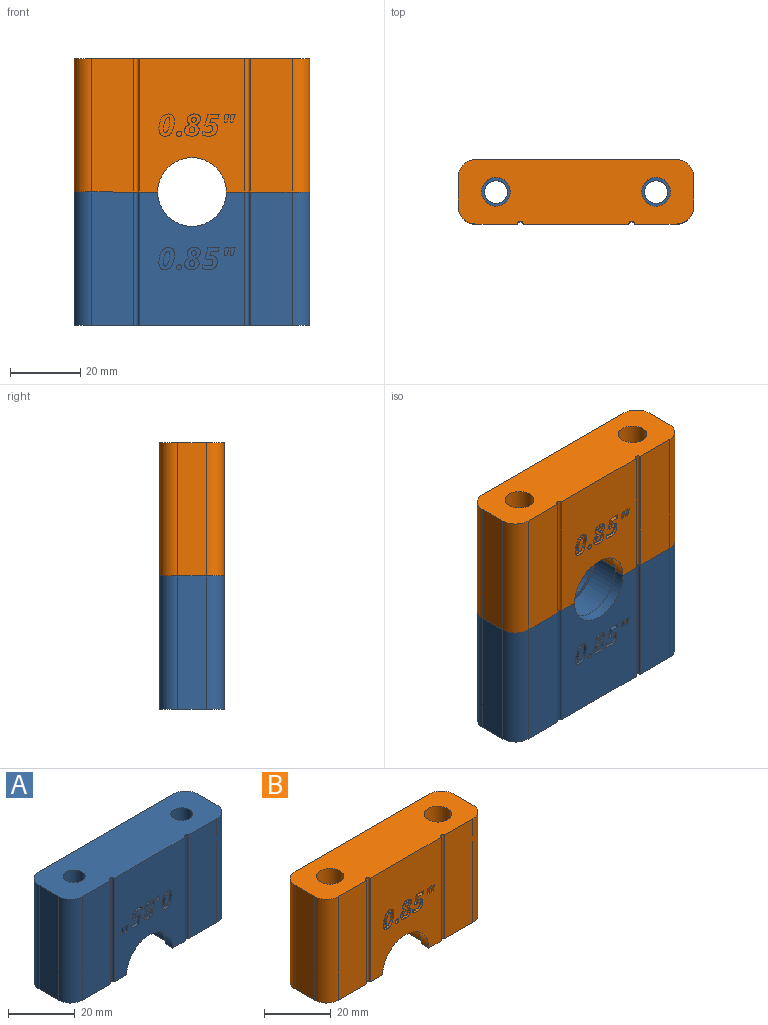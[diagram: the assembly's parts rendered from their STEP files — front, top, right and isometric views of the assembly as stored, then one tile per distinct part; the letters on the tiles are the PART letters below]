
ASSEMBLY  parts=2 mates=1
PART A: 116 faces, bbox 67.3x18.4x38.1 mm
  f0: plane 38.1x30.15mm, normal (0,-1,0), area 935mm2, adj f1,f2,f3,f13,f14,f15,f18,f19
  f1: plane 23.88x18.42mm, normal (0,0,-1), area 385.1mm2, adj f0,f5,f6,f7,f9,f10,f11,f12
  f2: plane 67.31x18.42mm, normal (0,0,1), area 1148.4mm2, adj f0,f4,f5,f7,f8,f10,f14,f15
  f3: plane 23.88x18.42mm, normal (0,0,-1), area 385.1mm2, adj f0,f4,f6,f8,f9,f10,f11,f12
  f4: plane 38.1x11.9mm, normal (0,-1,0), area 453.4mm2, adj f2,f3,f14,f112
  f5: plane 38.1x11.9mm, normal (0,-1,0), area 453.4mm2, adj f1,f2,f15,f113
  f6: plane 21.59x10.8mm, normal (0,-1,0), area 32.8mm2, adj f1,f3,f9,f11
  f7: plane 38.1x8.26mm, normal (1,0,0), area 314.5mm2, adj f1,f2,f113,f115
  f8: plane 38.1x8.26mm, normal (-1,0,0), area 314.5mm2, adj f2,f3,f112,f114
  f9: cylinder r=9.78mm len=19.56mm, axis (0,-1,0), area 195.1mm2, adj f1,f3,f6,f10
  f10: plane 57.15x38.1mm, normal (0,1,0), area 2027.2mm2, adj f1,f2,f3,f9,f114,f115
  f11: cylinder r=10.79mm len=21.59mm, axis (0,-1,0), area 301.5mm2, adj f1,f3,f6,f12
  f12: plane 21.59x10.8mm, normal (0,1,0), area 32.8mm2, adj f1,f3,f11,f13
  f13: cylinder r=9.78mm len=19.56mm, axis (0,-1,0), area 97.5mm2, adj f0,f1,f3,f12
  f14: cylinder r=0.8mm len=38.1mm, axis (0,0,-1), area 95.8mm2, adj f0,f2,f3,f4
  f15: cylinder r=0.8mm len=38.1mm, axis (0,0,-1), area 95.8mm2, adj f0,f1,f2,f5
  f16: cylinder r=3.26mm len=38.1mm, axis (0,0,-1), area 781.3mm2, adj f2,f3
  f17: cylinder r=3.26mm len=38.1mm, axis (0,0,-1), area 781.3mm2, adj f1,f2
  f18: plane 1.02x0.84mm, normal (0,0,-1), area 0.9mm2, adj f0,f19,f21,f22
  f19: plane 2.23x1.02mm, normal (0.96,0,-0.28), area 2.4mm2, adj f0,f18,f20,f22
  f20: plane 1.16x1.02mm, normal (0,0,1), area 1.2mm2, adj f0,f19,f21,f22
  f21: plane 2.23x1.02mm, normal (-0.99,0,0.14), area 2.3mm2, adj f0,f18,f20,f22
  f22: plane 2.23x1.48mm, normal (0,-1,0), area 2.2mm2, adj f18,f19,f20,f21
  f23: plane 1.02x0.83mm, normal (0,0,-1), area 0.8mm2, adj f0,f24,f26,f27
  f24: plane 2.23x1.02mm, normal (0.96,0,-0.28), area 2.4mm2, adj f0,f23,f25,f27
  f25: plane 1.17x1.02mm, normal (0,0,1), area 1.2mm2, adj f0,f24,f26,f27
  f26: plane 2.23x1.02mm, normal (-0.99,0,0.13), area 2.3mm2, adj f0,f23,f25,f27
  f27: plane 2.23x1.47mm, normal (0,-1,0), area 2.2mm2, adj f23,f24,f25,f26
  f28: extruded ~1.02x0.9mm, area 0.9mm2, adj f0,f29,f46,f49
  f29: extruded ~1.02x0.7mm, area 0.8mm2, adj f0,f28,f30,f49
  f30: extruded ~1.02x0.6mm, area 0.7mm2, adj f0,f29,f31,f49
  f31: extruded ~1.02x0.82mm, area 0.9mm2, adj f0,f30,f32,f49
  f32: extruded ~1.02x1.02mm, area 1.1mm2, adj f0,f31,f33,f49
  f33: extruded ~1.49x1.02mm, area 1.6mm2, adj f0,f32,f47,f49
  f34: extruded ~1.02x0.69mm, area 0.7mm2, adj f0,f35,f47,f49
  f35: extruded ~1.02x0.92mm, area 0.9mm2, adj f0,f34,f36,f49
  f36: extruded ~1.39x1.02mm, area 1.5mm2, adj f0,f35,f37,f49
  f37: extruded ~1.02x0.88mm, area 1.2mm2, adj f0,f36,f38,f49
  f38: extruded ~1.23x1.02mm, area 1.3mm2, adj f0,f37,f39,f49
  f39: extruded ~1.21x1.02mm, area 1.3mm2, adj f0,f38,f40,f49
  f40: extruded ~1.22x1.02mm, area 1.3mm2, adj f0,f39,f41,f49
  f41: extruded ~1.02x0.54mm, area 0.5mm2, adj f0,f40,f48,f49
  f42: plane 2.06x1.02mm, normal (0,0,-1), area 2.1mm2, adj f0,f43,f48,f49
  f43: plane 1.11x1.02mm, normal (0.98,0,-0.21), area 1.1mm2, adj f0,f42,f44,f49
  f44: plane 3.18x1.02mm, normal (0,0,1), area 3.2mm2, adj f0,f43,f45,f49
  f45: plane 3.09x1.02mm, normal (-0.96,0,0.27), area 3.3mm2, adj f0,f44,f46,f49
  f46: plane 1.02x0.44mm, normal (-0.6,0,-0.8), area 0.6mm2, adj f0,f28,f45,f49
  f47: plane 1.13x1.02mm, normal (-1,0,0), area 1.2mm2, adj f0,f33,f34,f49
  f48: plane 1.24x1.02mm, normal (0.96,0,-0.29), area 1.3mm2, adj f0,f41,f42,f49
  f49: plane 6.25x4.65mm, normal (0,-1,0), area 14.3mm2, adj f28,f29,f30,f31,f32,f33,f34,f35
  f50: extruded ~1.02x0.9mm, area 1mm2, adj f0,f51,f79,f80
  f51: extruded ~1.26x1.02mm, area 1.5mm2, adj f0,f50,f52,f80
  f52: extruded ~1.8x1.47mm, area 2.5mm2, adj f0,f51,f53,f80
  f53: extruded ~1.14x1.02mm, area 1.3mm2, adj f0,f52,f54,f80
  f54: extruded ~1.42x1.02mm, area 1.5mm2, adj f0,f53,f55,f80
  f55: extruded ~1.15x1.02mm, area 1.2mm2, adj f0,f54,f56,f80
  f56: extruded ~1.02x0.76mm, area 1mm2, adj f0,f55,f57,f80
  f57: extruded ~1.02x0.92mm, area 1mm2, adj f0,f56,f58,f80
  f58: extruded ~1.54x1.02mm, area 1.9mm2, adj f0,f57,f59,f80
  f59: extruded ~1.02x0.97mm, area 1.2mm2, adj f0,f58,f60,f80
  f60: extruded ~1.02x0.99mm, area 1.1mm2, adj f0,f59,f61,f80
  f61: extruded ~1.02x0.73mm, area 0.8mm2, adj f0,f60,f62,f80
  f62: extruded ~1.02x0.59mm, area 0.8mm2, adj f0,f61,f63,f80
  f63: extruded ~1.02x0.91mm, area 0.9mm2, adj f0,f62,f64,f80
  f64: extruded ~1.08x1.02mm, area 1.1mm2, adj f0,f63,f79,f80
  f65: extruded ~1.02x0.58mm, area 0.7mm2, adj f66,f78,f80,f81
  f66: extruded ~1.02x0.62mm, area 0.7mm2, adj f65,f67,f80,f81
  f67: extruded ~1.02x0.57mm, area 0.6mm2, adj f66,f68,f80,f81
  f68: extruded ~1.02x0.54mm, area 0.6mm2, adj f67,f69,f80,f81
  f69: extruded ~1.02x0.65mm, area 0.7mm2, adj f68,f70,f80,f81
  f70: extruded ~1.02x0.73mm, area 0.9mm2, adj f69,f71,f80,f81
  f71: extruded ~1.02x0.51mm, area 0.7mm2, adj f70,f78,f80,f81
  f72: extruded ~1.02x0.93mm, area 1.3mm2, adj f73,f77,f80,f82
  f73: extruded ~1.02x0.85mm, area 1.1mm2, adj f72,f74,f80,f82
  f74: extruded ~1.02x0.5mm, area 0.6mm2, adj f73,f75,f80,f82
  f75: extruded ~1.02x0.51mm, area 0.6mm2, adj f74,f76,f80,f82
  f76: extruded ~1.02x0.43mm, area 0.5mm2, adj f75,f77,f80,f82
  f77: extruded ~1.02x0.45mm, area 0.5mm2, adj f72,f76,f80,f82
  f78: extruded ~1.02x0.56mm, area 0.6mm2, adj f65,f71,f80,f81
  f79: extruded ~1.02x0.71mm, area 1mm2, adj f0,f50,f64,f80
  f80: plane 6.35x4.52mm, normal (0,-1,0), area 16.9mm2, adj f50,f51,f52,f53,f54,f55,f56,f57
  f81: plane 1.84x1.63mm, normal (0,-1,0), area 2.3mm2, adj f65,f66,f67,f68,f69,f70,f71,f78
  f82: plane 1.55x1.3mm, normal (0,-1,0), area 1.5mm2, adj f72,f73,f74,f75,f76,f77
  f83: extruded ~1.02x0.61mm, area 0.7mm2, adj f0,f84,f90,f91
  f84: extruded ~1.02x0.59mm, area 0.7mm2, adj f0,f83,f85,f91
  f85: extruded ~1.02x0.45mm, area 0.5mm2, adj f0,f84,f86,f91
  f86: extruded ~1.02x0.46mm, area 0.5mm2, adj f0,f85,f87,f91
  f87: extruded ~1.02x0.64mm, area 0.7mm2, adj f0,f86,f88,f91
  f88: extruded ~1.02x0.61mm, area 0.7mm2, adj f0,f87,f89,f91
  f89: extruded ~1.02x0.44mm, area 0.5mm2, adj f0,f88,f90,f91
  f90: extruded ~1.02x0.48mm, area 0.5mm2, adj f0,f83,f89,f91
  f91: plane 1.49x1.43mm, normal (0,-1,0), area 1.7mm2, adj f83,f84,f85,f86,f87,f88,f89,f90
  f92: extruded ~1.52x1.02mm, area 1.9mm2, adj f0,f93,f109,f110
  f93: extruded ~2.27x1.02mm, area 2.3mm2, adj f0,f92,f94,f110
  f94: extruded ~1.54x1.02mm, area 1.7mm2, adj f0,f93,f95,f110
  f95: extruded ~1.27x1.02mm, area 1.4mm2, adj f0,f94,f96,f110
  f96: extruded ~1.99x1.19mm, area 2.5mm2, adj f0,f95,f97,f110
  f97: extruded ~3.17x1.02mm, area 3.3mm2, adj f0,f96,f98,f110
  f98: extruded ~2x1.68mm, area 3mm2, adj f0,f97,f109,f110
  f99: extruded ~1.63x1.02mm, area 1.7mm2, adj f100,f108,f110,f111
  f100: extruded ~1.27x1.02mm, area 1.4mm2, adj f99,f101,f110,f111
  f101: extruded ~1.02x0.63mm, area 0.8mm2, adj f100,f102,f110,f111
  f102: extruded ~1.02x0.41mm, area 0.5mm2, adj f101,f103,f110,f111
  f103: extruded ~1.02x0.73mm, area 0.8mm2, adj f102,f104,f110,f111
  f104: extruded ~1.55x1.02mm, area 1.6mm2, adj f103,f105,f110,f111
  f105: extruded ~1.27x1.02mm, area 1.4mm2, adj f104,f106,f110,f111
  f106: extruded ~1.02x0.63mm, area 0.8mm2, adj f105,f107,f110,f111
  f107: extruded ~1.02x0.39mm, area 0.5mm2, adj f106,f108,f110,f111
  f108: extruded ~1.02x0.68mm, area 0.7mm2, adj f99,f107,f110,f111
  f109: extruded ~1.41x1.02mm, area 1.6mm2, adj f0,f92,f98,f110
  f110: plane 6.35x4.4mm, normal (0,-1,0), area 16.7mm2, adj f92,f93,f94,f95,f96,f97,f98,f99
  f111: plane 4.24x1.85mm, normal (0,-1,0), area 5.6mm2, adj f99,f100,f101,f102,f103,f104,f105,f106
  f112: cylinder r=5.08mm len=38.1mm, axis (0,0,-1), area 304mm2, adj f2,f3,f4,f8
  f113: cylinder r=5.08mm len=38.1mm, axis (0,0,1), area 304mm2, adj f1,f2,f5,f7
  f114: cylinder r=5.08mm len=38.1mm, axis (0,0,1), area 304mm2, adj f2,f3,f8,f10
  f115: cylinder r=5.08mm len=38.1mm, axis (0,0,-1), area 304mm2, adj f1,f2,f7,f10
PART B: 116 faces, bbox 67.3x18.4x38.1 mm
  f0: plane 38.1x30.15mm, normal (0,-1,0), area 935mm2, adj f1,f2,f3,f13,f14,f15,f18,f19
  f1: plane 23.88x18.42mm, normal (0,0,-1), area 365.7mm2, adj f0,f5,f6,f7,f9,f10,f11,f12
  f2: plane 67.31x18.42mm, normal (0,0,1), area 1109.6mm2, adj f0,f4,f5,f7,f8,f10,f14,f15
  f3: plane 23.88x18.42mm, normal (0,0,-1), area 365.7mm2, adj f0,f4,f6,f8,f9,f10,f11,f12
  f4: plane 38.1x11.9mm, normal (0,-1,0), area 453.4mm2, adj f2,f3,f14,f112
  f5: plane 38.1x11.9mm, normal (0,-1,0), area 453.4mm2, adj f1,f2,f15,f113
  f6: plane 21.59x10.8mm, normal (0,-1,0), area 32.8mm2, adj f1,f3,f9,f11
  f7: plane 38.1x8.26mm, normal (1,0,0), area 314.5mm2, adj f1,f2,f113,f115
  f8: plane 38.1x8.26mm, normal (-1,0,0), area 314.5mm2, adj f2,f3,f112,f114
  f9: cylinder r=9.78mm len=19.56mm, axis (0,-1,0), area 195.1mm2, adj f1,f3,f6,f10
  f10: plane 57.15x38.1mm, normal (0,1,0), area 2027.2mm2, adj f1,f2,f3,f9,f114,f115
  f11: cylinder r=10.79mm len=21.59mm, axis (0,-1,0), area 301.5mm2, adj f1,f3,f6,f12
  f12: plane 21.59x10.8mm, normal (0,1,0), area 32.8mm2, adj f1,f3,f11,f13
  f13: cylinder r=9.78mm len=19.56mm, axis (0,-1,0), area 97.5mm2, adj f0,f1,f3,f12
  f14: cylinder r=0.8mm len=38.1mm, axis (0,0,-1), area 95.8mm2, adj f0,f2,f3,f4
  f15: cylinder r=0.8mm len=38.1mm, axis (0,0,-1), area 95.8mm2, adj f0,f1,f2,f5
  f16: cylinder r=4.1mm len=38.1mm, axis (0,0,-1), area 982mm2, adj f2,f3
  f17: cylinder r=4.1mm len=38.1mm, axis (0,0,-1), area 982mm2, adj f1,f2
  f18: plane 1.02x0.84mm, normal (0,0,1), area 0.9mm2, adj f0,f19,f21,f22
  f19: plane 2.23x1.02mm, normal (-0.96,0,0.28), area 2.4mm2, adj f0,f18,f20,f22
  f20: plane 1.16x1.02mm, normal (0,0,-1), area 1.2mm2, adj f0,f19,f21,f22
  f21: plane 2.23x1.02mm, normal (0.99,0,-0.14), area 2.3mm2, adj f0,f18,f20,f22
  f22: plane 2.23x1.48mm, normal (0,-1,0), area 2.2mm2, adj f18,f19,f20,f21
  f23: plane 1.02x0.83mm, normal (0,0,1), area 0.8mm2, adj f0,f24,f26,f27
  f24: plane 2.23x1.02mm, normal (-0.96,0,0.28), area 2.4mm2, adj f0,f23,f25,f27
  f25: plane 1.17x1.02mm, normal (0,0,-1), area 1.2mm2, adj f0,f24,f26,f27
  f26: plane 2.23x1.02mm, normal (0.99,0,-0.13), area 2.3mm2, adj f0,f23,f25,f27
  f27: plane 2.23x1.47mm, normal (0,-1,0), area 2.2mm2, adj f23,f24,f25,f26
  f28: extruded ~1.02x0.9mm, area 0.9mm2, adj f0,f29,f46,f49
  f29: extruded ~1.02x0.7mm, area 0.8mm2, adj f0,f28,f30,f49
  f30: extruded ~1.02x0.6mm, area 0.7mm2, adj f0,f29,f31,f49
  f31: extruded ~1.02x0.82mm, area 0.9mm2, adj f0,f30,f32,f49
  f32: extruded ~1.02x1.02mm, area 1.1mm2, adj f0,f31,f33,f49
  f33: extruded ~1.49x1.02mm, area 1.6mm2, adj f0,f32,f47,f49
  f34: extruded ~1.02x0.69mm, area 0.7mm2, adj f0,f35,f47,f49
  f35: extruded ~1.02x0.92mm, area 0.9mm2, adj f0,f34,f36,f49
  f36: extruded ~1.39x1.02mm, area 1.5mm2, adj f0,f35,f37,f49
  f37: extruded ~1.02x0.88mm, area 1.2mm2, adj f0,f36,f38,f49
  f38: extruded ~1.23x1.02mm, area 1.3mm2, adj f0,f37,f39,f49
  f39: extruded ~1.21x1.02mm, area 1.3mm2, adj f0,f38,f40,f49
  f40: extruded ~1.22x1.02mm, area 1.3mm2, adj f0,f39,f41,f49
  f41: extruded ~1.02x0.54mm, area 0.5mm2, adj f0,f40,f48,f49
  f42: plane 2.06x1.02mm, normal (0,0,1), area 2.1mm2, adj f0,f43,f48,f49
  f43: plane 1.11x1.02mm, normal (-0.98,0,0.21), area 1.1mm2, adj f0,f42,f44,f49
  f44: plane 3.18x1.02mm, normal (0,0,-1), area 3.2mm2, adj f0,f43,f45,f49
  f45: plane 3.09x1.02mm, normal (0.96,0,-0.27), area 3.3mm2, adj f0,f44,f46,f49
  f46: plane 1.02x0.44mm, normal (0.6,0,0.8), area 0.6mm2, adj f0,f28,f45,f49
  f47: plane 1.13x1.02mm, normal (1,0,0), area 1.2mm2, adj f0,f33,f34,f49
  f48: plane 1.24x1.02mm, normal (-0.96,0,0.29), area 1.3mm2, adj f0,f41,f42,f49
  f49: plane 6.25x4.65mm, normal (0,-1,0), area 14.3mm2, adj f28,f29,f30,f31,f32,f33,f34,f35
  f50: extruded ~1.02x0.9mm, area 1mm2, adj f0,f51,f79,f80
  f51: extruded ~1.26x1.02mm, area 1.5mm2, adj f0,f50,f52,f80
  f52: extruded ~1.8x1.47mm, area 2.5mm2, adj f0,f51,f53,f80
  f53: extruded ~1.14x1.02mm, area 1.3mm2, adj f0,f52,f54,f80
  f54: extruded ~1.42x1.02mm, area 1.5mm2, adj f0,f53,f55,f80
  f55: extruded ~1.15x1.02mm, area 1.2mm2, adj f0,f54,f56,f80
  f56: extruded ~1.02x0.76mm, area 1mm2, adj f0,f55,f57,f80
  f57: extruded ~1.02x0.92mm, area 1mm2, adj f0,f56,f58,f80
  f58: extruded ~1.54x1.02mm, area 1.9mm2, adj f0,f57,f59,f80
  f59: extruded ~1.02x0.97mm, area 1.2mm2, adj f0,f58,f60,f80
  f60: extruded ~1.02x0.99mm, area 1.1mm2, adj f0,f59,f61,f80
  f61: extruded ~1.02x0.73mm, area 0.8mm2, adj f0,f60,f62,f80
  f62: extruded ~1.02x0.59mm, area 0.8mm2, adj f0,f61,f63,f80
  f63: extruded ~1.02x0.91mm, area 0.9mm2, adj f0,f62,f64,f80
  f64: extruded ~1.08x1.02mm, area 1.1mm2, adj f0,f63,f79,f80
  f65: extruded ~1.02x0.58mm, area 0.7mm2, adj f66,f78,f80,f81
  f66: extruded ~1.02x0.62mm, area 0.7mm2, adj f65,f67,f80,f81
  f67: extruded ~1.02x0.57mm, area 0.6mm2, adj f66,f68,f80,f81
  f68: extruded ~1.02x0.54mm, area 0.6mm2, adj f67,f69,f80,f81
  f69: extruded ~1.02x0.65mm, area 0.7mm2, adj f68,f70,f80,f81
  f70: extruded ~1.02x0.73mm, area 0.9mm2, adj f69,f71,f80,f81
  f71: extruded ~1.02x0.51mm, area 0.7mm2, adj f70,f78,f80,f81
  f72: extruded ~1.02x0.93mm, area 1.3mm2, adj f73,f77,f80,f82
  f73: extruded ~1.02x0.85mm, area 1.1mm2, adj f72,f74,f80,f82
  f74: extruded ~1.02x0.5mm, area 0.6mm2, adj f73,f75,f80,f82
  f75: extruded ~1.02x0.51mm, area 0.6mm2, adj f74,f76,f80,f82
  f76: extruded ~1.02x0.43mm, area 0.5mm2, adj f75,f77,f80,f82
  f77: extruded ~1.02x0.45mm, area 0.5mm2, adj f72,f76,f80,f82
  f78: extruded ~1.02x0.56mm, area 0.6mm2, adj f65,f71,f80,f81
  f79: extruded ~1.02x0.71mm, area 1mm2, adj f0,f50,f64,f80
  f80: plane 6.35x4.52mm, normal (0,-1,0), area 16.9mm2, adj f50,f51,f52,f53,f54,f55,f56,f57
  f81: plane 1.84x1.63mm, normal (0,-1,0), area 2.3mm2, adj f65,f66,f67,f68,f69,f70,f71,f78
  f82: plane 1.55x1.3mm, normal (0,-1,0), area 1.5mm2, adj f72,f73,f74,f75,f76,f77
  f83: extruded ~1.02x0.61mm, area 0.7mm2, adj f0,f84,f90,f91
  f84: extruded ~1.02x0.59mm, area 0.7mm2, adj f0,f83,f85,f91
  f85: extruded ~1.02x0.45mm, area 0.5mm2, adj f0,f84,f86,f91
  f86: extruded ~1.02x0.46mm, area 0.5mm2, adj f0,f85,f87,f91
  f87: extruded ~1.02x0.64mm, area 0.7mm2, adj f0,f86,f88,f91
  f88: extruded ~1.02x0.61mm, area 0.7mm2, adj f0,f87,f89,f91
  f89: extruded ~1.02x0.44mm, area 0.5mm2, adj f0,f88,f90,f91
  f90: extruded ~1.02x0.48mm, area 0.5mm2, adj f0,f83,f89,f91
  f91: plane 1.49x1.43mm, normal (0,-1,0), area 1.7mm2, adj f83,f84,f85,f86,f87,f88,f89,f90
  f92: extruded ~1.52x1.02mm, area 1.9mm2, adj f0,f93,f109,f110
  f93: extruded ~2.27x1.02mm, area 2.3mm2, adj f0,f92,f94,f110
  f94: extruded ~1.54x1.02mm, area 1.7mm2, adj f0,f93,f95,f110
  f95: extruded ~1.27x1.02mm, area 1.4mm2, adj f0,f94,f96,f110
  f96: extruded ~1.99x1.19mm, area 2.5mm2, adj f0,f95,f97,f110
  f97: extruded ~3.17x1.02mm, area 3.3mm2, adj f0,f96,f98,f110
  f98: extruded ~2x1.68mm, area 3mm2, adj f0,f97,f109,f110
  f99: extruded ~1.63x1.02mm, area 1.7mm2, adj f100,f108,f110,f111
  f100: extruded ~1.27x1.02mm, area 1.4mm2, adj f99,f101,f110,f111
  f101: extruded ~1.02x0.63mm, area 0.8mm2, adj f100,f102,f110,f111
  f102: extruded ~1.02x0.41mm, area 0.5mm2, adj f101,f103,f110,f111
  f103: extruded ~1.02x0.73mm, area 0.8mm2, adj f102,f104,f110,f111
  f104: extruded ~1.55x1.02mm, area 1.6mm2, adj f103,f105,f110,f111
  f105: extruded ~1.27x1.02mm, area 1.4mm2, adj f104,f106,f110,f111
  f106: extruded ~1.02x0.63mm, area 0.8mm2, adj f105,f107,f110,f111
  f107: extruded ~1.02x0.39mm, area 0.5mm2, adj f106,f108,f110,f111
  f108: extruded ~1.02x0.68mm, area 0.7mm2, adj f99,f107,f110,f111
  f109: extruded ~1.41x1.02mm, area 1.6mm2, adj f0,f92,f98,f110
  f110: plane 6.35x4.4mm, normal (0,-1,0), area 16.7mm2, adj f92,f93,f94,f95,f96,f97,f98,f99
  f111: plane 4.24x1.85mm, normal (0,-1,0), area 5.6mm2, adj f99,f100,f101,f102,f103,f104,f105,f106
  f112: cylinder r=5.08mm len=38.1mm, axis (0,0,-1), area 304mm2, adj f2,f3,f4,f8
  f113: cylinder r=5.08mm len=38.1mm, axis (0,0,1), area 304mm2, adj f1,f2,f5,f7
  f114: cylinder r=5.08mm len=38.1mm, axis (0,0,1), area 304mm2, adj f2,f3,f8,f10
  f115: cylinder r=5.08mm len=38.1mm, axis (0,0,-1), area 304mm2, adj f1,f2,f7,f10
PLACE A rot(axis=(0,-1,0),180deg) t=(-13.65,-6.78,49.71)mm fixed
PLACE B rot(axis=(0,1,0),0deg) t=(-13.65,-6.78,49.71)mm
MATE slider A.f16 <-> B.f17  axis (0,0,1) through (9.21,2.43,49.71)mm
